# Revit family: RAD010021
name_source: partatom
category: Luminaires
revit_build: Autodesk Revit Architecture 2015 (Build: 20140223_1515(x64)
units: mm (PartAtom-declared; Revit-internal decimal feet)

## types (1)
- Radian Team LED Encastré Longueur 600
    Adresse = 5ter rue d'Arsonval - 75015 Paris - France
    Commentaires du type = Options : Gradation, système de gestion par cellule centrale, température de couleur : 3000K ou 4000K. Autre connecteur : nous consulter. Ailettes décoratives RAL 9003
    Description = Appareillage électronique pour 1 module LED de 9W maximum et d'une efficacité lumineuse de 140 lm/w
    Emettre à partir de la longueur de la ligne = 575 mm
    Fabricant = Radian
    Fax = 0033 (0)1 43 21 72 61
    Filtre de couleur = 16777215
    Finition = Radian
    Gradation des changements de température de couleur de lampe = <Aucun>
    Hauteur = 43
    Information = Français
    Intensité lumineuse = 96 lm/w
    Largeur = 80
    Light = Radian Light
    Longueur = 596
    Matériaux et finitions = Moteur LED en aluminium extrudé laqué blanc. Ailettes décoratives en acier couleur nickel. Optique spéciale a contrôle de luminance pour une uniformité supérieure à 0,8 en polycarbonate injecté. Kit chantier (filin de sécurité, connecteur LINECT, film de protection)
    Metal = Acier inoxydable, poli
    Modèle = Réf. 930
    Normes = NF EN 60-598 - NF EN 55015 - NF EN 61547
    Palette RAL = Blanc RAL 9003
    Paramètres = Langue
    Polantis code = RAD010021
    Puissance = 12W
    Taille du symbole de la source d'éclairage = 600 mm  [stored 1.9685 ft]
    URL = www.radian.fr

note: [stored X ft] marks values corroborated as IEEE doubles in the binary element streams (Revit-internal decimal feet)

## geometry (parser evidence)
native form markers: Sweep x3
no freeform markers — native parametric forms only
